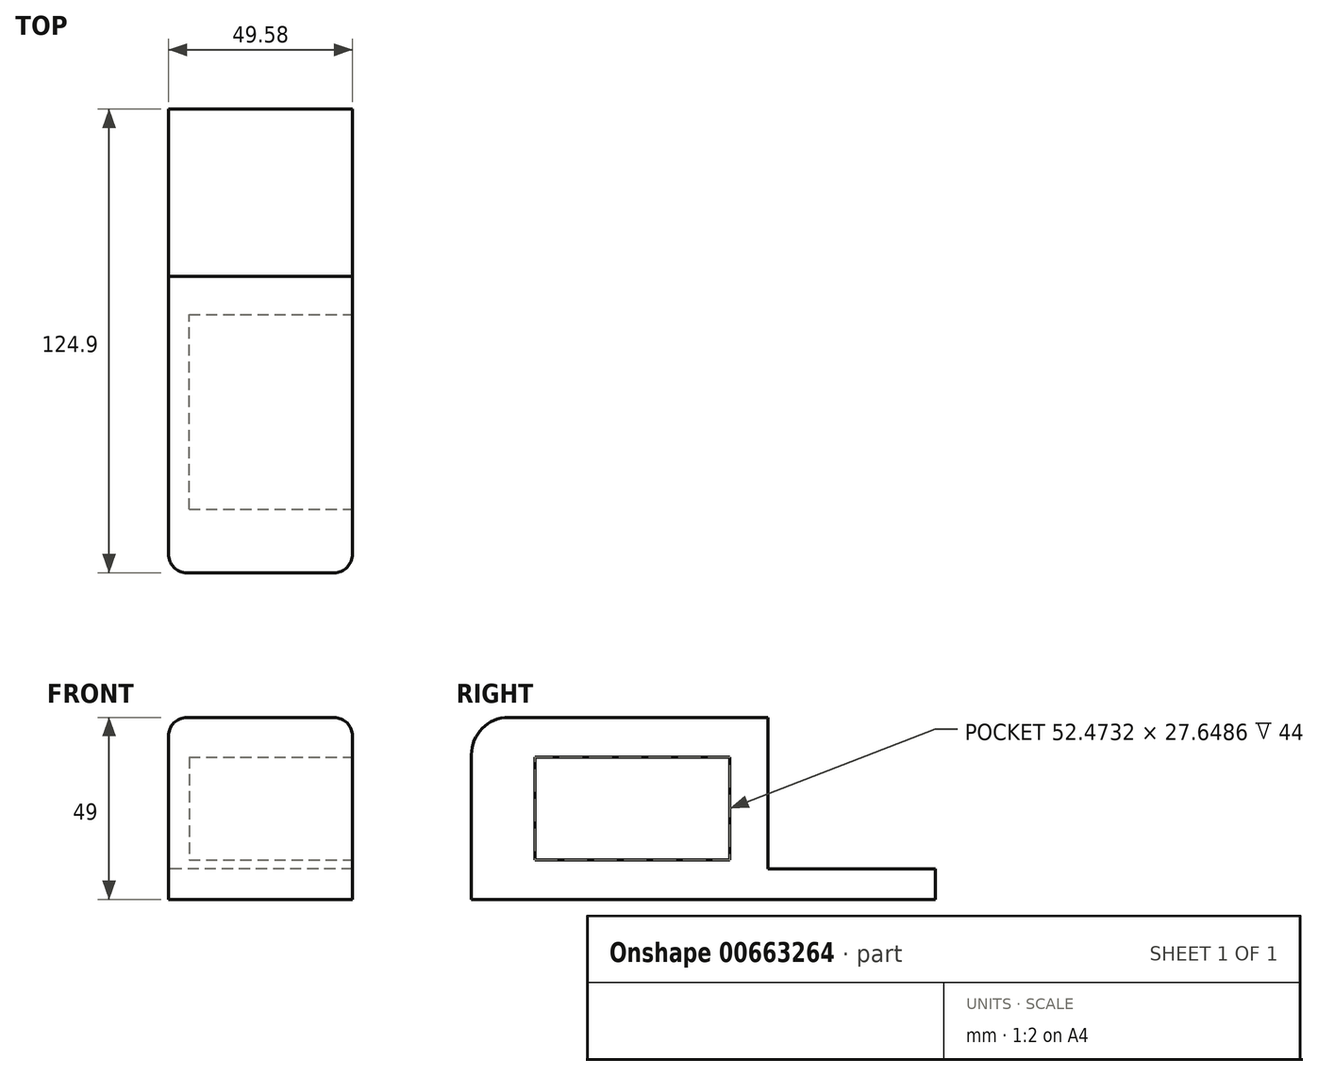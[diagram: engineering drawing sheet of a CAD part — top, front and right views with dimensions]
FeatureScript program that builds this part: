
annotation { "Feature Type Name" : "Feature", "Feature Type Description" : "" }
export const myFeature = defineFeature(function(context is Context, id is Id, definition is map)
    precondition{}
    {
        {
            var Q0;
            Q0=qCreatedBy(makeId("Front.planeOp"),FACE);
            var sketch = newSketch(context, id + "F0", { "sketchPlane" : qUnion([Q0])});
            skLineSegment(sketch, "E0.bottom", {"start": v(24.79, -24.5) * mm, "end": v(-24.79, -24.5) * mm});
            skLineSegment(sketch, "E0.top", {"start": v(24.79, 24.5) * mm, "end": v(-24.79, 24.5) * mm});
            skLineSegment(sketch, "E0.left", {"start": v(24.79, -24.5) * mm, "end": v(24.79, 24.5) * mm});
            skLineSegment(sketch, "E0.right", {"start": v(-24.79, -24.5) * mm, "end": v(-24.79, 24.5) * mm});
            skPoint(sketch, "E0.middle", {"position": v(0, 0) * mm});
            skSolve(sketch);
        }
        {
            var Q0;
            Q0=makeQuery(id+"F0.imprint","IMPRINT",FACE,{"disambiguationData":[TD([[makeQuery(id+"F0.imprint","IMPRINT",EDGE,{"derivedFrom":sQuery(id+"F0.wireOp",EDGE,"E0.bottom")}),-1.0]])]});
            extrude(context, id + "F1", {"entities" : qUnion([Q0]), "oppositeDirection" : true, "depth" : 79.9 * mm, "offsetDistance" : 25 * mm});
        }
        {
            var Q0;
            Q0=makeQuery(id+"F1.opExtrude","CAP_FACE",FACE,{"disambiguationData":[OSD([sQuery(id+"F0.wireOp",EDGE,"E0.bottom"),sQuery(id+"F0.wireOp",EDGE,"E0.top"),sQuery(id+"F0.wireOp",EDGE,"E0.left"),sQuery(id+"F0.wireOp",EDGE,"E0.right")])],"isStart":false});
            var sketch = newSketch(context, id + "F2", { "sketchPlane" : qUnion([Q0])});
            skLineSegment(sketch, "E1.bottom", {"start": v(-24.79, -24.5) * mm, "end": v(24.79, -24.5) * mm});
            skLineSegment(sketch, "E1.top", {"start": v(-24.79, -16.29) * mm, "end": v(24.79, -16.29) * mm});
            skLineSegment(sketch, "E1.left", {"start": v(-24.79, -24.5) * mm, "end": v(-24.79, -16.29) * mm});
            skLineSegment(sketch, "E1.right", {"start": v(24.79, -24.5) * mm, "end": v(24.79, -16.29) * mm});
            skSolve(sketch);
        }
        {
            var Q0;
            Q0=makeQuery(id+"F2.imprint","IMPRINT",FACE,{"disambiguationData":[TD([[makeQuery(id+"F2.imprint","IMPRINT",EDGE,{"derivedFrom":sQuery(id+"F2.wireOp",EDGE,"E1.bottom")}),1.0]])]});
            extrude(context, id + "F3", {"entities" : qUnion([Q0]), "operationType" : NewBodyOperationType.ADD, "depth" : 45 * mm, "offsetDistance" : 25 * mm});
        }
        {
            var Q0;
            Q0=makeQuery(id+"F1.opExtrude","CAP_EDGE",EDGE,{"disambiguationData":[OSD([sQuery(id+"F0.wireOp",EDGE,"E0.top")])],"isStart":true});
            fillet(context, id + "F4", {"entities" : qUnion([Q0]), "radius" : 10 * mm, "tangentPropagation" : true, "allowEdgeOverflow" : false});
        }
        {
            var Q0;
            Q0=makeQuery(id+"F4.opFillet","BLEND_EDGE",EDGE,{"blendedFrom":[makeQuery(id+"F1.opExtrude","CAP_EDGE",EDGE,{"disambiguationData":[OSD([sQuery(id+"F0.wireOp",EDGE,"E0.top")])],"isStart":true}),makeQuery(id+"F3.boolean.opBoolean","MERGE",FACE,{"derivedFrom":[makeQuery(id+"F1.opExtrude","SWEPT_FACE",FACE,{"disambiguationData":[OSD([sQuery(id+"F0.wireOp",EDGE,"E0.left")])]}),makeQuery(id+"F3.opExtrude","SWEPT_FACE",FACE,{"disambiguationData":[OSD([sQuery(id+"F2.wireOp",EDGE,"E1.left")])]})]})],"blendedInto":[makeQuery(id+"F3.boolean.opBoolean","MERGE",FACE,{"derivedFrom":[makeQuery(id+"F1.opExtrude","SWEPT_FACE",FACE,{"disambiguationData":[OSD([sQuery(id+"F0.wireOp",EDGE,"E0.left")])]}),makeQuery(id+"F3.opExtrude","SWEPT_FACE",FACE,{"disambiguationData":[OSD([sQuery(id+"F2.wireOp",EDGE,"E1.left")])]})]})]});
            var Q1;
            Q1=makeQuery(id+"F4.opFillet","BLEND_EDGE",EDGE,{"blendedFrom":[makeQuery(id+"F1.opExtrude","CAP_EDGE",EDGE,{"disambiguationData":[OSD([sQuery(id+"F0.wireOp",EDGE,"E0.top")])],"isStart":true}),makeQuery(id+"F3.boolean.opBoolean","MERGE",FACE,{"derivedFrom":[makeQuery(id+"F1.opExtrude","SWEPT_FACE",FACE,{"disambiguationData":[OSD([sQuery(id+"F0.wireOp",EDGE,"E0.right")])]}),makeQuery(id+"F3.opExtrude","SWEPT_FACE",FACE,{"disambiguationData":[OSD([sQuery(id+"F2.wireOp",EDGE,"E1.right")])]})]})],"blendedInto":[makeQuery(id+"F3.boolean.opBoolean","MERGE",FACE,{"derivedFrom":[makeQuery(id+"F1.opExtrude","SWEPT_FACE",FACE,{"disambiguationData":[OSD([sQuery(id+"F0.wireOp",EDGE,"E0.right")])]}),makeQuery(id+"F3.opExtrude","SWEPT_FACE",FACE,{"disambiguationData":[OSD([sQuery(id+"F2.wireOp",EDGE,"E1.right")])]})]})]});
            fillet(context, id + "F5", {"entities" : qUnion([Q0, Q1]), "radius" : 5 * mm, "tangentPropagation" : true, "allowEdgeOverflow" : false});
        }
        {
            var Q0;
            Q0=makeQuery(id+"F3.boolean.opBoolean","MERGE",FACE,{"derivedFrom":[makeQuery(id+"F1.opExtrude","SWEPT_FACE",FACE,{"disambiguationData":[OSD([sQuery(id+"F0.wireOp",EDGE,"E0.left")])]}),makeQuery(id+"F3.opExtrude","SWEPT_FACE",FACE,{"disambiguationData":[OSD([sQuery(id+"F2.wireOp",EDGE,"E1.left")])]})]});
            var sketch = newSketch(context, id + "F6", { "sketchPlane" : qUnion([Q0])});
            skPoint(sketch, "E2", {"position": v(19.53, -10.06) * mm});
            skSolve(sketch);
        }
        {
            var Q0;
            {var subQ0=sQuery(id+"F2.wireOp",EDGE,"E1.left");Q0=makeQuery(id+"F6.imprint","IMPRINT",FACE,{"disambiguationData":[TD([[makeQuery(id+"F6.imprint","IMPRINT",EDGE,{"derivedFrom":makeQuery(id+"F3.opExtrude","CAP_EDGE",EDGE,{"disambiguationData":[OSD([subQ0])],"isStart":false})}),1.0]])]});}
            var sketch = newSketch(context, id + "F7", { "sketchPlane" : qUnion([Q0])});
            skLineSegment(sketch, "E3.bottom", {"start": v(17.09, 13.82) * mm, "end": v(69.56, 13.82) * mm});
            skLineSegment(sketch, "E3.top", {"start": v(17.09, -13.83) * mm, "end": v(69.56, -13.83) * mm});
            skLineSegment(sketch, "E3.left", {"start": v(17.09, 13.82) * mm, "end": v(17.09, -13.83) * mm});
            skLineSegment(sketch, "E3.right", {"start": v(69.56, 13.82) * mm, "end": v(69.56, -13.83) * mm});
            skSolve(sketch);
        }
        {
            var Q0;
            Q0 = qSketchRegion(id + "F7", true);
            extrude(context, id + "F8", {"entities" : qUnion([Q0]), "operationType" : NewBodyOperationType.REMOVE, "oppositeDirection" : true, "depth" : 44 * mm, "offsetDistance" : 25 * mm});
        }
    });
